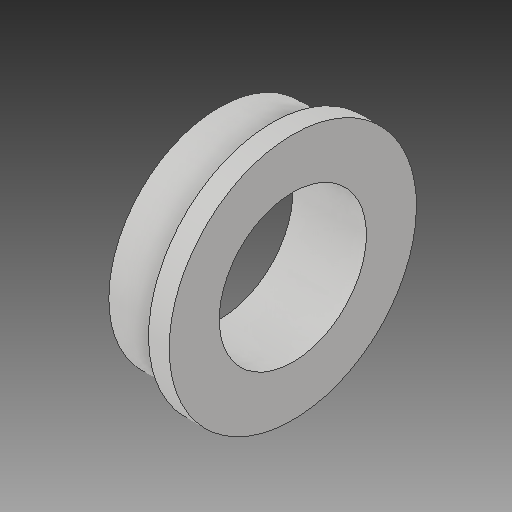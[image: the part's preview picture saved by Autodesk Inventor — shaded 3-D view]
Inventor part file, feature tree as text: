
AUTODESK INVENTOR PART (.ipt)
format: ipt  version: 2019 (Build 230136000, 136)  size: 114,688 bytes
history: native  units: in
note: dims shown in document units (in); Inventor stores cm internally (conversion verified against a paired STEP export)
features: revolve x1, sketch x1
ambient origin geometry x8: Origin, YZ Plane, XZ Plane, XY Plane, X Axis, Y Axis, Z Axis, Center Point
bodies: Solid1 (feature_tree)
feature tree (2):
  revolve  "Revolution1"  [1 undecoded]
  sketch  "Sketch1"  dims[d0=0.25in d1=0.375in d2=0.42in d3=0.09in d4=0.035in d5=90.0deg]
note: 1 required parameter value undecoded (feature->parameter linkage not recoverable at this tier; creation-order binding heuristic only, values carry confidence <= 0.55)
